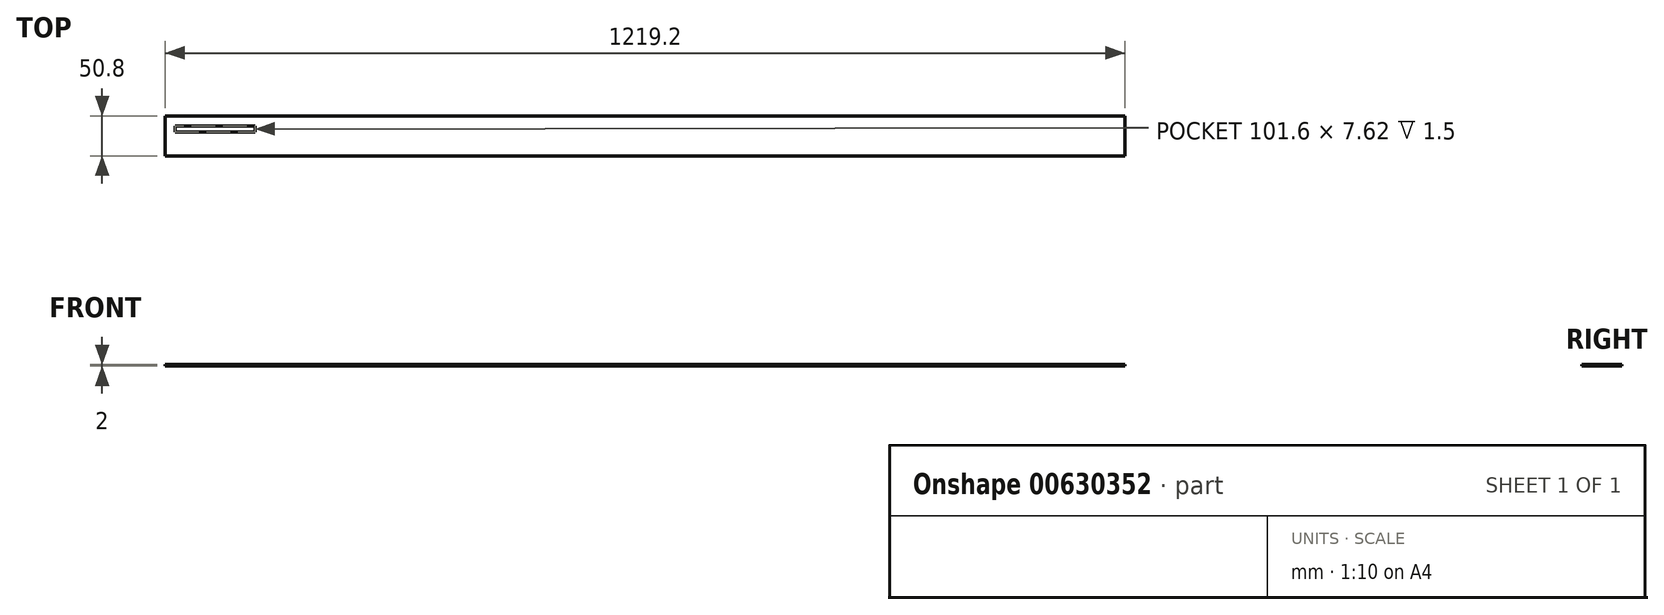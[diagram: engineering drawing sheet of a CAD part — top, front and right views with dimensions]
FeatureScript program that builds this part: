
annotation { "Feature Type Name" : "Feature", "Feature Type Description" : "" }
export const myFeature = defineFeature(function(context is Context, id is Id, definition is map)
    precondition{}
    {
        {
            assignVariable(context, id + "F0", {"name" : "patte_largeur", "anyValue" : 2});
        }
        {
            assignVariable(context, id + "F1", {"name" : "mortaise_haut", "anyValue" : 0.5});
        }
        {
            assignVariable(context, id + "F2", {"name" : "mortaise_largeur", "anyValue" : 4});
        }
        {
            assignVariable(context, id + "F3", {"name" : "mortaise_profondeur", "anyValue" : 1.5});
        }
        {
            var Q0;
            Q0=qCreatedBy(makeId("Top.planeOp"),FACE);
            var sketch = newSketch(context, id + "F4", { "sketchPlane" : qUnion([Q0])});
            skLineSegment(sketch, "E0.bottom", {"start": v(-609.6, 25.4) * mm, "end": v(609.6, 25.4) * mm});
            skLineSegment(sketch, "E0.top", {"start": v(-609.6, -25.4) * mm, "end": v(609.6, -25.4) * mm});
            skLineSegment(sketch, "E0.left", {"start": v(-609.6, 25.4) * mm, "end": v(-609.6, -25.4) * mm});
            skLineSegment(sketch, "E0.right", {"start": v(609.6, 25.4) * mm, "end": v(609.6, -25.4) * mm});
            skSolve(sketch);
        }
        {
            var Q0;
            Q0 = qSketchRegion(id + "F4", true);
            extrude(context, id + "F5", {"entities" : qUnion([Q0]), "endBound" : BoundingType.SYMMETRIC, "depth" : (getVariable(context, 'patte_largeur')) * mm, "offsetDistance" : 25.4 * mm});
        }
        {
            var Q0;
            Q0=makeQuery(id+"F5.opExtrude","SWEPT_FACE",FACE,{"disambiguationData":[OSD([sQuery(id+"F4.wireOp",EDGE,"E0.left")])]});
            cPlane(context, id + "F6", {"entities" : qUnion([Q0]), "cplaneType" : CPlaneType.OFFSET, "offset" : (getVariable(context, 'mortaise_haut')) * mm, "oppositeDirection" : true, "width" : 152.4 * mm, "height" : 152.4 * mm});
        }
        {
            var Q0;
            Q0=makeQuery(id+"F5.opExtrude","SWEPT_FACE",FACE,{"disambiguationData":[OSD([sQuery(id+"F4.wireOp",EDGE,"E0.left")])]});
            cPlane(context, id + "F7", {"entities" : qUnion([Q0]), "cplaneType" : CPlaneType.OFFSET, "offset" : (getVariable(context, 'mortaise_largeur') + getVariable(context, 'mortaise_haut')) * mm, "oppositeDirection" : true, "width" : 152.4 * mm, "height" : 152.4 * mm});
        }
        {
            var Q0;
            Q0=makeQuery(id+"F5.opExtrude","CAP_VERTEX",VERTEX,{"disambiguationData":[OSD([sQuery(id+"F4.wireOp",EDGE,"E0.top"),sQuery(id+"F4.wireOp",EDGE,"E0.left")])],"isStart":false});
            var Q1;
            Q1=makeQuery(id+"F5.opExtrude","CAP_VERTEX",VERTEX,{"disambiguationData":[OSD([sQuery(id+"F4.wireOp",EDGE,"E0.bottom"),sQuery(id+"F4.wireOp",EDGE,"E0.left")])],"isStart":true});
            var Q2;
            Q2=makeQuery(id+"F5.opExtrude","CAP_VERTEX",VERTEX,{"disambiguationData":[OSD([sQuery(id+"F4.wireOp",EDGE,"E0.bottom"),sQuery(id+"F4.wireOp",EDGE,"E0.right")])],"isStart":true});
            cPlane(context, id + "F8", {"entities" : qUnion([Q0, Q1, Q2]), "cplaneType" : CPlaneType.THREE_POINT, "offset" : 25.4 * mm, "width" : 152.4 * mm, "height" : 152.4 * mm});
        }
        {
            var Q0;
            Q0=makeQuery(id+"F5.opExtrude","CAP_FACE",FACE,{"disambiguationData":[OSD([sQuery(id+"F4.wireOp",EDGE,"E0.bottom"),sQuery(id+"F4.wireOp",EDGE,"E0.top"),sQuery(id+"F4.wireOp",EDGE,"E0.left"),sQuery(id+"F4.wireOp",EDGE,"E0.right")])],"isStart":false});
            var sketch = newSketch(context, id + "F9", { "sketchPlane" : qUnion([Q0])});
            skLineSegment(sketch, "E1.bottom", {"start": v(-596.9, 12.7) * mm, "end": v(-495.3, 12.7) * mm});
            skLineSegment(sketch, "E1.top", {"start": v(-596.9, 5.08) * mm, "end": v(-495.3, 5.08) * mm});
            skLineSegment(sketch, "E1.left", {"start": v(-596.9, 12.7) * mm, "end": v(-596.9, 5.08) * mm});
            skLineSegment(sketch, "E1.right", {"start": v(-495.3, 12.7) * mm, "end": v(-495.3, 5.08) * mm});
            skSolve(sketch);
        }
        {
            var Q0;
            Q0=makeQuery(id+"F9.imprint","IMPRINT",FACE,{"disambiguationData":[TD([[makeQuery(id+"F9.imprint","IMPRINT",EDGE,{"derivedFrom":sQuery(id+"F9.wireOp",EDGE,"E1.bottom")}),-1.0]])]});
            extrude(context, id + "F10", {"entities" : qUnion([Q0]), "operationType" : NewBodyOperationType.REMOVE, "oppositeDirection" : true, "depth" : (getVariable(context, 'mortaise_profondeur')) * mm, "offsetDistance" : 25.4 * mm});
        }
    });
